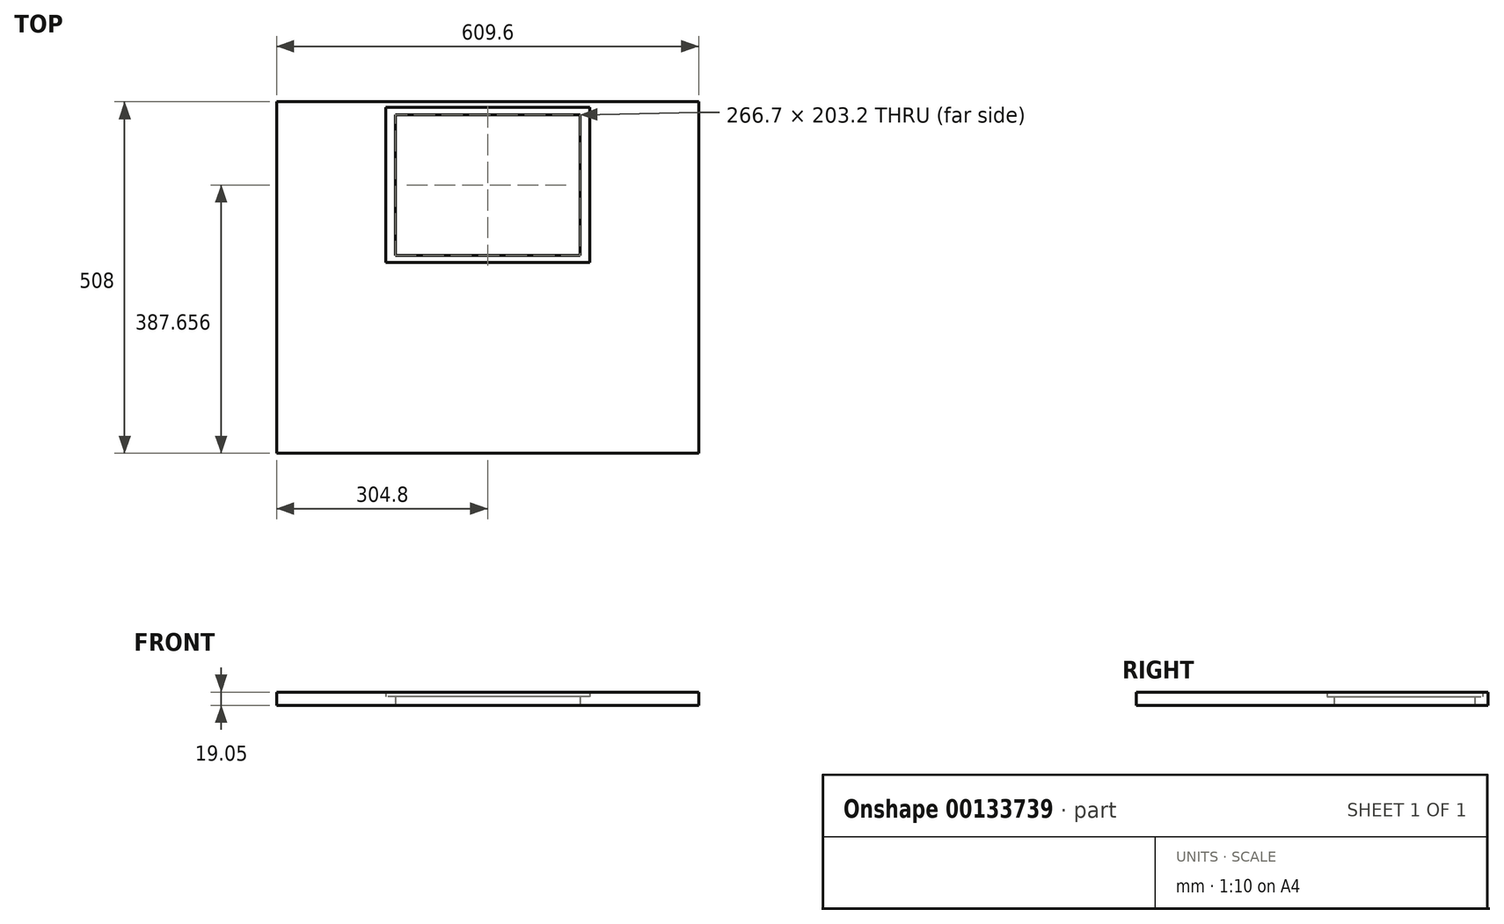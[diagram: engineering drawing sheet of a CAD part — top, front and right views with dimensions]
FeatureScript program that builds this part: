
annotation { "Feature Type Name" : "Feature", "Feature Type Description" : "" }
export const myFeature = defineFeature(function(context is Context, id is Id, definition is map)
    precondition{}
    {
        {
            var Q0;
            Q0=qCreatedBy(makeId("Top.planeOp"),FACE);
            var sketch = newSketch(context, id + "F0", { "sketchPlane" : qUnion([Q0])});
            skLineSegment(sketch, "E0.bottom", {"start": v(304.8, -254) * mm, "end": v(-304.8, -254) * mm});
            skLineSegment(sketch, "E0.top", {"start": v(304.8, 254) * mm, "end": v(-304.8, 254) * mm});
            skLineSegment(sketch, "E0.left", {"start": v(304.8, -254) * mm, "end": v(304.8, 254) * mm});
            skLineSegment(sketch, "E0.right", {"start": v(-304.8, -254) * mm, "end": v(-304.8, 254) * mm});
            skPoint(sketch, "E0.middle", {"position": v(0, 0) * mm});
            skLineSegment(sketch, "E1.bottom", {"start": v(133.35, 32.06) * mm, "end": v(-133.35, 32.06) * mm});
            skLineSegment(sketch, "E1.top", {"start": v(133.35, 235.26) * mm, "end": v(-133.35, 235.26) * mm});
            skLineSegment(sketch, "E1.left", {"start": v(133.35, 32.06) * mm, "end": v(133.35, 235.26) * mm});
            skLineSegment(sketch, "E1.right", {"start": v(-133.35, 32.06) * mm, "end": v(-133.35, 235.26) * mm});
            skPoint(sketch, "E1.middle", {"position": v(0, 133.66) * mm});
            skSolve(sketch);
        }
        {
            var Q0;
            Q0 = qSketchRegion(id + "F0", true);
            extrude(context, id + "F1", {"entities" : qUnion([Q0]), "depth" : 12.7 * mm});
        }
        {
            var Q0;
            Q0=makeQuery(id+"F1.opExtrude","CAP_FACE",FACE,{"disambiguationData":[OSD([sQuery(id+"F0.wireOp",EDGE,"E0.bottom"),sQuery(id+"F0.wireOp",EDGE,"E0.top"),sQuery(id+"F0.wireOp",EDGE,"E0.left"),sQuery(id+"F0.wireOp",EDGE,"E0.right"),sQuery(id+"F0.wireOp",EDGE,"E1.bottom"),sQuery(id+"F0.wireOp",EDGE,"E1.top"),sQuery(id+"F0.wireOp",EDGE,"E1.left"),sQuery(id+"F0.wireOp",EDGE,"E1.right")])],"isStart":false});
            var sketch = newSketch(context, id + "F2", { "sketchPlane" : qUnion([Q0])});
            skLineSegment(sketch, "E2.bottom", {"start": v(147.3, 21.8) * mm, "end": v(-147.3, 21.8) * mm});
            skLineSegment(sketch, "E2.top", {"start": v(147.3, 246.1) * mm, "end": v(-147.3, 246.1) * mm});
            skLineSegment(sketch, "E2.left", {"start": v(147.3, 21.8) * mm, "end": v(147.3, 246.1) * mm});
            skLineSegment(sketch, "E2.right", {"start": v(-147.3, 21.8) * mm, "end": v(-147.3, 246.1) * mm});
            skPoint(sketch, "E2.middle", {"position": v(0, 133.95) * mm});
            skSolve(sketch);
        }
        {
            var Q0;
            Q0=makeQuery(id+"F2.imprint","IMPRINT",FACE,{"disambiguationData":[TD([[makeQuery(id+"F2.imprint","IMPRINT",EDGE,{"derivedFrom":sQuery(id+"F2.wireOp",EDGE,"E2.bottom")}),1.0]])]});
            extrude(context, id + "F3", {"entities" : qUnion([Q0]), "operationType" : NewBodyOperationType.ADD, "depth" : 6.35 * mm});
        }
    });
